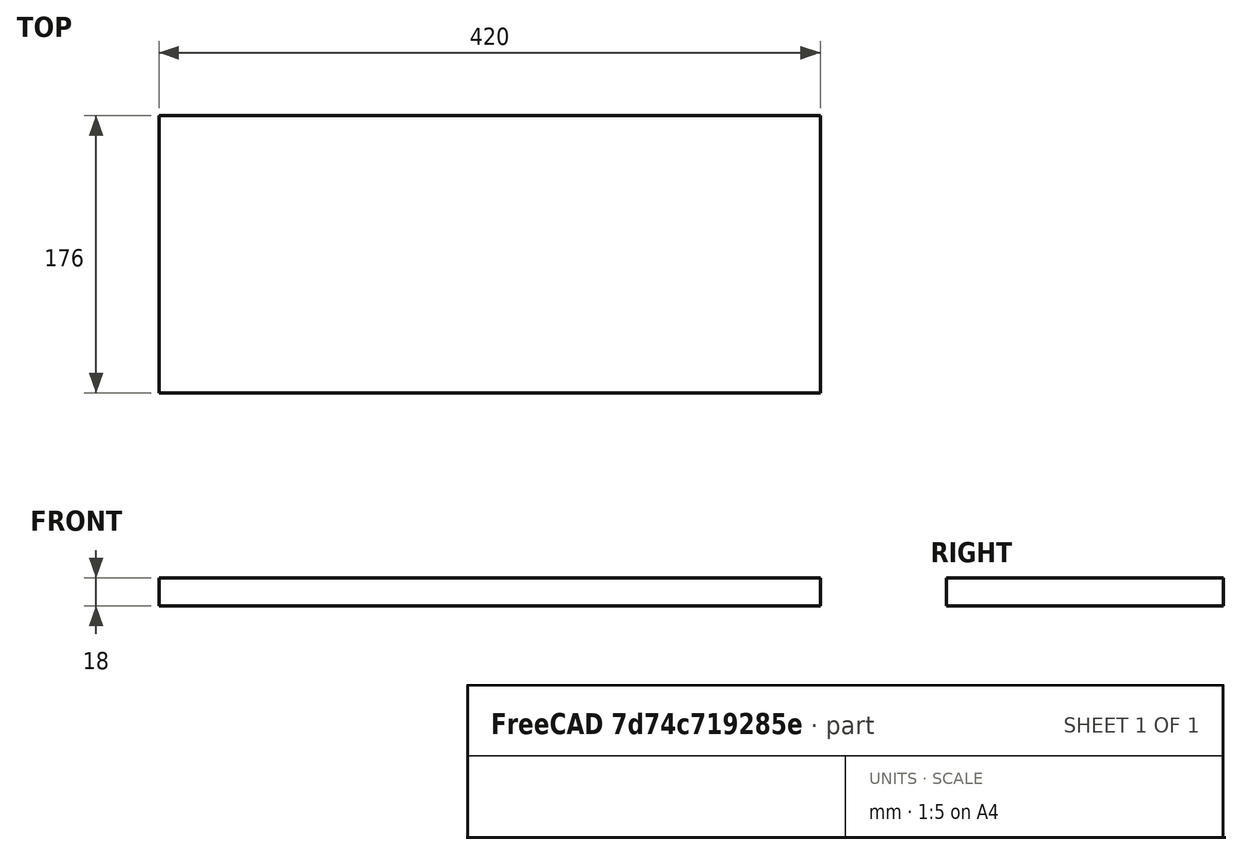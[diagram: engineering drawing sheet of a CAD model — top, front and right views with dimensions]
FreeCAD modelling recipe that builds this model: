
FCSTD DOCUMENT  (FreeCAD 0.18R4 (GitTag))
Label: bottom_shelf_2
License: All rights reserved
LicenseURL: http://en.wikipedia.org/wiki/All_rights_reserved
objects: Sketcher::SketchObject×1, PartDesign::Pad×1, PartDesign::Body×1
note: 4 computed .brp shape members not serialized (recipe doc carries the construction recipe); baked Part::Feature solids carry a one-line shape summary decoded from their .brp

FEATURE [Sketcher::SketchObject] Sketch
  MapMode = 5
  Support = -> [XY_Plane]
  sketch-geometry (4):
    g0: LineSegment StartX=0 StartY=0 StartZ=0 EndX=-420 EndY=0 EndZ=0
    g1: LineSegment StartX=-420 StartY=0 StartZ=0 EndX=-420 EndY=176 EndZ=0
    g2: LineSegment StartX=-420 StartY=176 StartZ=0 EndX=0 EndY=176 EndZ=0
    g3: LineSegment StartX=0 StartY=176 StartZ=0 EndX=0 EndY=0 EndZ=0
  constraints (11):
    c: Coincident(g0,g1)
    c: Coincident(g1,g2)
    c: Coincident(g2,g3)
    c: Coincident(g3,g0)
    c: Horizontal(g0)
    c: Horizontal(g2)
    c: Vertical(g1)
    c: Vertical(g3)
    c: Coincident(g0,g-1)
    c: DistanceX(g0,g0) = 420
    c: DistanceY(g3,g3) = 176
FEATURE [PartDesign::Pad] Pad
  Length = 18
  Length2 = 100
  Profile = -> Sketch
  Type = 0
FEATURE [PartDesign::Body] Body
  Group = -> [Sketch,Pad]
  Origin = -> Origin
  Tip = -> Pad
